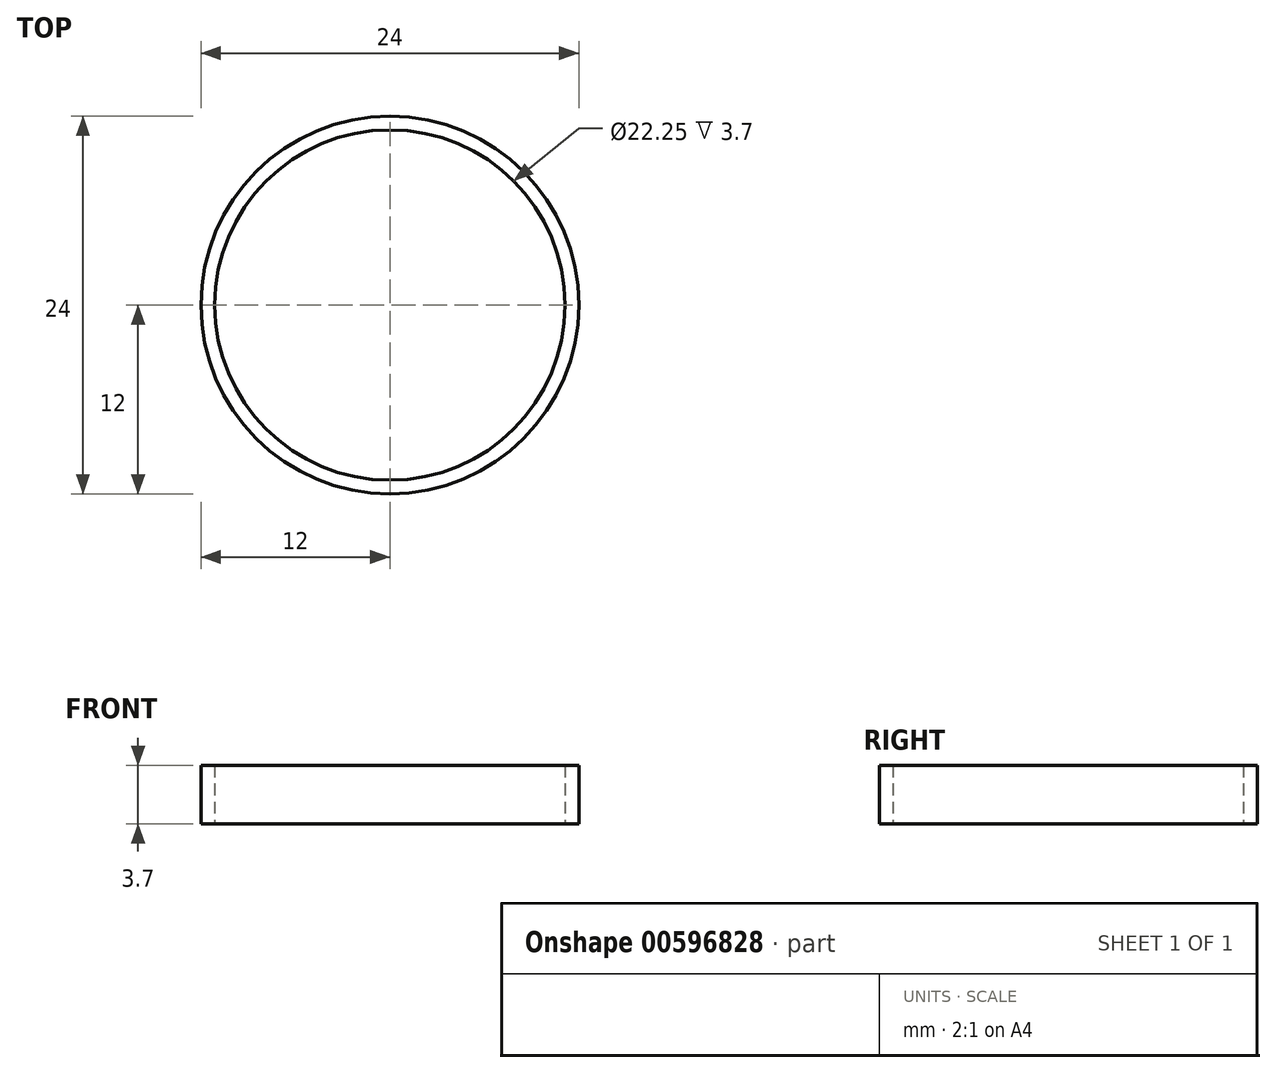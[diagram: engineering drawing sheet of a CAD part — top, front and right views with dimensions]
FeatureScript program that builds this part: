
annotation { "Feature Type Name" : "Feature", "Feature Type Description" : "" }
export const myFeature = defineFeature(function(context is Context, id is Id, definition is map)
    precondition{}
    {
        {
            var Q0;
            Q0=qCreatedBy(makeId("Top.planeOp"),FACE);
            var sketch = newSketch(context, id + "F0", { "sketchPlane" : qUnion([Q0])});
            skCircle(sketch, "E0", {"center": v(0, 0) * mm, "radius": 12 * mm});
            skCircle(sketch, "E1", {"center": v(0, 0) * mm, "radius": 11.12 * mm});
            skSolve(sketch);
        }
        {
            var Q0;
            Q0=makeQuery(id+"F0.imprint","IMPRINT",FACE,{"disambiguationData":[TD([[makeQuery(id+"F0.imprint","IMPRINT",EDGE,{"derivedFrom":sQuery(id+"F0.wireOp",EDGE,"E0")}),1.0]])]});
            extrude(context, id + "F1", {"entities" : qUnion([Q0]), "depth" : 3.7 * mm, "offsetDistance" : 25 * mm});
        }
    });
